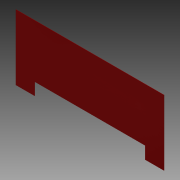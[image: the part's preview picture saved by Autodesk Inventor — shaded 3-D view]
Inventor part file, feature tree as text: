
AUTODESK INVENTOR PART (.ipt)
format: ipt  version: 2013 (Build 170138000, 138)  size: 77,312 bytes
history: native  units: in
note: dims shown in document units (in); Inventor stores cm internally (conversion verified against a paired STEP export)
features: extrude x1, sketch x1
ambient origin geometry x8: Origin, YZ Plane, XZ Plane, XY Plane, X Axis, Y Axis, Z Axis, Center Point
bodies: Solid1 (feature_tree)
feature tree (2):
  extrude  "Extrusion1"  Depth=32.0in
  sketch  "Sketch1"  dims[d0=72.5in d1=32.0in d2=9.25in d3=6.0in d4=9.25in d5=6.0in d6=0.125in d7=0.0in]
